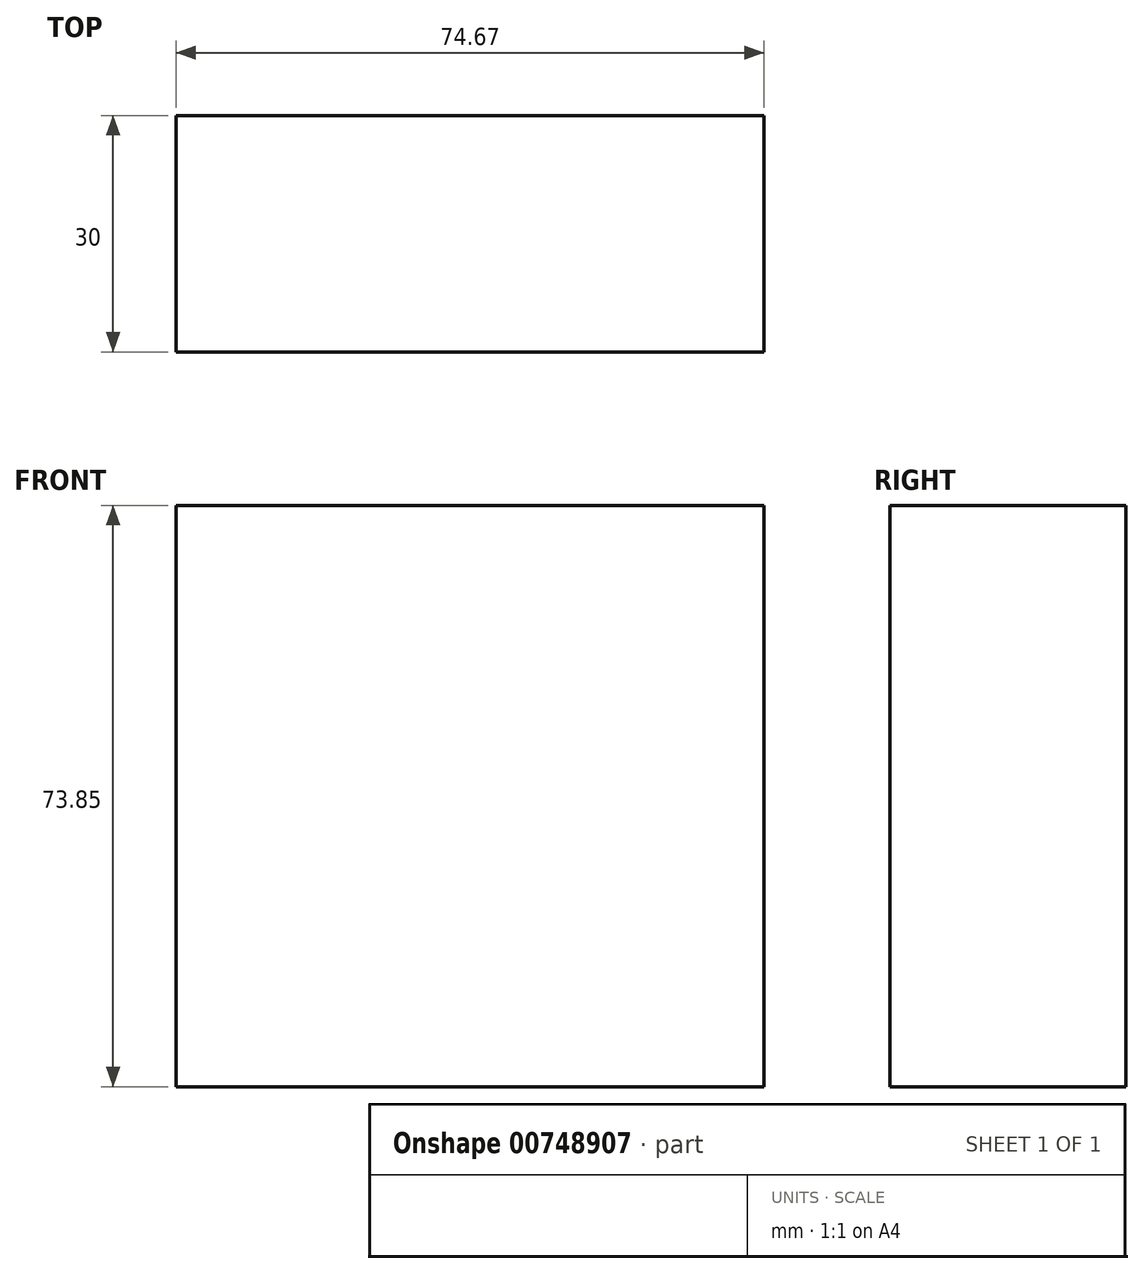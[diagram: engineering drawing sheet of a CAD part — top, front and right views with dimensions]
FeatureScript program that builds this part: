
annotation { "Feature Type Name" : "Feature", "Feature Type Description" : "" }
export const myFeature = defineFeature(function(context is Context, id is Id, definition is map)
    precondition{}
    {
        {
            var Q0;
            Q0=qCreatedBy(makeId("Front.planeOp"),FACE);
            var sketch = newSketch(context, id + "F0", { "sketchPlane" : qUnion([Q0])});
            skLineSegment(sketch, "E0.bottom", {"start": v(-33.44, 37.95) * mm, "end": v(41.23, 37.95) * mm});
            skLineSegment(sketch, "E0.top", {"start": v(-33.44, -35.9) * mm, "end": v(41.23, -35.9) * mm});
            skLineSegment(sketch, "E0.left", {"start": v(-33.44, 37.95) * mm, "end": v(-33.44, -35.9) * mm});
            skLineSegment(sketch, "E0.right", {"start": v(41.23, 37.95) * mm, "end": v(41.23, -35.9) * mm});
            skSolve(sketch);
        }
        {
            var Q0;
            Q0 = qSketchRegion(id + "F0", true);
            extrude(context, id + "F1", {"entities" : qUnion([Q0]), "oppositeDirection" : true, "depth" : 30 * mm, "offsetDistance" : 25 * mm});
        }
    });
